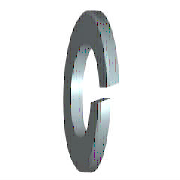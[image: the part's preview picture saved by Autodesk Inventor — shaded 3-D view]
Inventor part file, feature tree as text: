
AUTODESK INVENTOR PART (.ipt)
format: ipt  version: 2025 (Build 290162000, 162)  size: 126,464 bytes
history: native  units: mm (DEFAULTED — no unit token found)
features: extrude x2, other x1, plane x1
ambient origin geometry x6: Origin, YZ Plane, X Axis, Y Axis, Z Axis, Center Point
bodies: Solid1 (feature_tree)
feature tree (4):
  extrude  "轴承体"  Depth=12.2mm
  extrude  "切口"  Depth=18.4mm
  other  "Work Axis1"
  plane  "Work Plane1"
